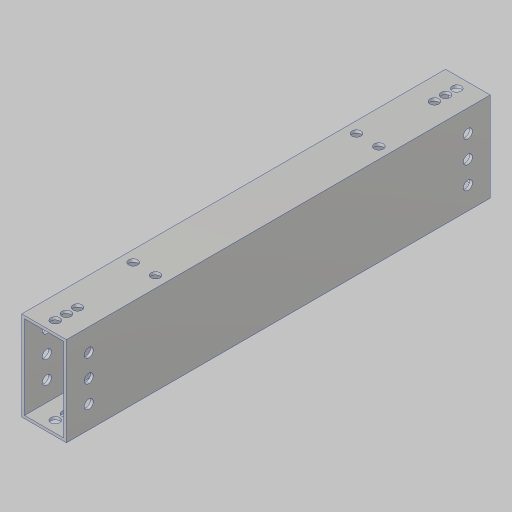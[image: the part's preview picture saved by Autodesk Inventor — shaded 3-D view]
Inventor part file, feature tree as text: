
AUTODESK INVENTOR PART (.ipt)
format: ipt  version: 2023.5 (Build 275446000, 446)  size: 175,616 bytes
history: native  units: in
note: dims shown in document units (in); Inventor stores cm internally (conversion verified against a paired STEP export)
features: hole x3, sketch x3, extrude x1, mirror x1, projected_geometry x1
ambient origin geometry x8: Origin, YZ Plane, XZ Plane, XY Plane, X Axis, Y Axis, Z Axis, Center Point
bodies: Solid1 (feature_tree)
feature tree (9):
  extrude  "Extrusion1"  Depth=0.5in
  hole  "Hole1"  [1 undecoded]
  hole  "Hole2"  [1 undecoded]
  hole  "Hole3"  [1 undecoded]
  mirror  "Mirror1"
  sketch  "Sketch2"  dims[d4=0.0in d5=0.5in]
  sketch  "Sketch3"  dims[d6=0.5in d7=0.5in]
  sketch  "Sketch4"  dims[d8=0.5in d9=0.5in d10=0.5in d11=0.201in d12=0.75in d13=0.385in d14=0.25in d15=0.5635in d16=1.0in d17=0.8108in d18=0.25in d19=0.25in d20=0.25in d21=0.5in d22=0.25in d23=0.25in d24=0.25in d25=0.201in d26=0.75in d27=0.385in d28=0.25in d29=0.5635in d30=1.0in d31=0.8108in d32=0.5in d33=2.0in d34=1.245in d35=0.201in d36=0.38in d37=0.385in d38=0.25in d39=0.5635in d40=1.0in d41=0.8108in]
  projected_geometry  "Project Cut Edges1"
note: 3 required parameter values undecoded (feature->parameter linkage not recoverable at this tier; creation-order binding heuristic only, values carry confidence <= 0.55)
